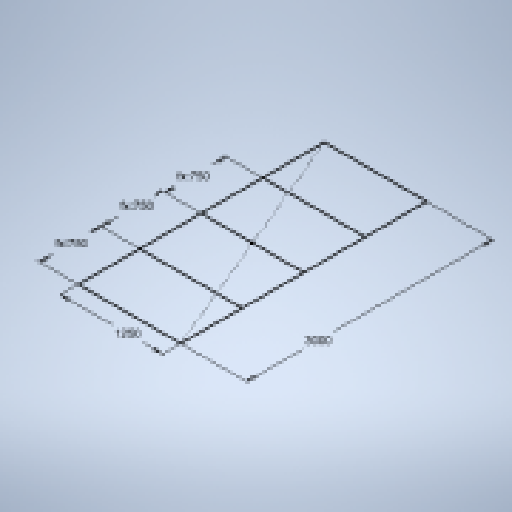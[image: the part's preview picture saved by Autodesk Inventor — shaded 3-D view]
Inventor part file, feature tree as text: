
AUTODESK INVENTOR PART (.ipt)
format: ipt  version: 2025 (Build 290162010, 162A)  size: 268,288 bytes
history: native  units: in
note: dims shown in document units (in); Inventor stores cm internally (conversion verified against a paired STEP export)
features: sketch x1
ambient origin geometry x8: Origin, YZ Plane, XZ Plane, XY Plane, X Axis, Y Axis, Z Axis, Center Point
feature tree (1):
  sketch  "Sketch3"  dims[d7=49.2126in d8=118.1102in d9=29.5276in d10=29.5276in d11=29.5276in]
